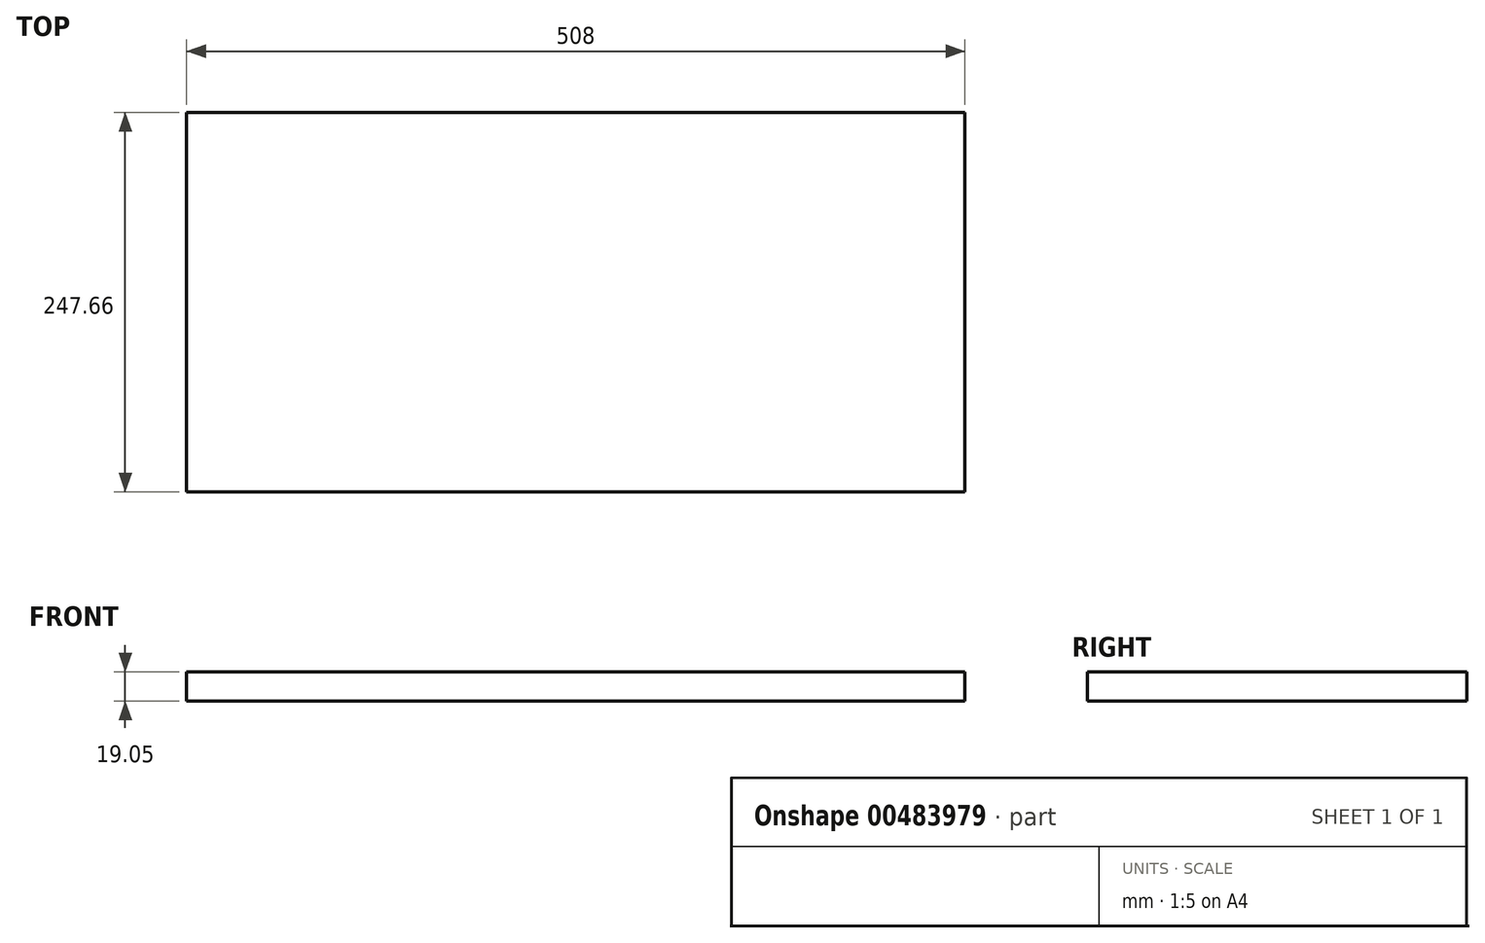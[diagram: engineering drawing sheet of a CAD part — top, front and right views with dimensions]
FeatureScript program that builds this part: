
annotation { "Feature Type Name" : "Feature", "Feature Type Description" : "" }
export const myFeature = defineFeature(function(context is Context, id is Id, definition is map)
    precondition{}
    {
        {
            var Q0;
            Q0=qCreatedBy(makeId("Top.planeOp"),FACE);
            var sketch = newSketch(context, id + "F0", { "sketchPlane" : qUnion([Q0])});
            skLineSegment(sketch, "E0.bottom", {"start": v(254, -123.82) * mm, "end": v(-254, -123.83) * mm});
            skLineSegment(sketch, "E0.top", {"start": v(254, 123.83) * mm, "end": v(-254, 123.83) * mm});
            skLineSegment(sketch, "E0.left", {"start": v(254, -123.82) * mm, "end": v(254, 123.83) * mm});
            skLineSegment(sketch, "E0.right", {"start": v(-254, -123.83) * mm, "end": v(-254, 123.83) * mm});
            skPoint(sketch, "E0.middle", {"position": v(0, 0) * mm});
            skSolve(sketch);
        }
        {
            var Q0;
            Q0 = qSketchRegion(id + "F0", true);
            extrude(context, id + "F1", {"entities" : qUnion([Q0]), "depth" : 19.05 * mm});
        }
    });
